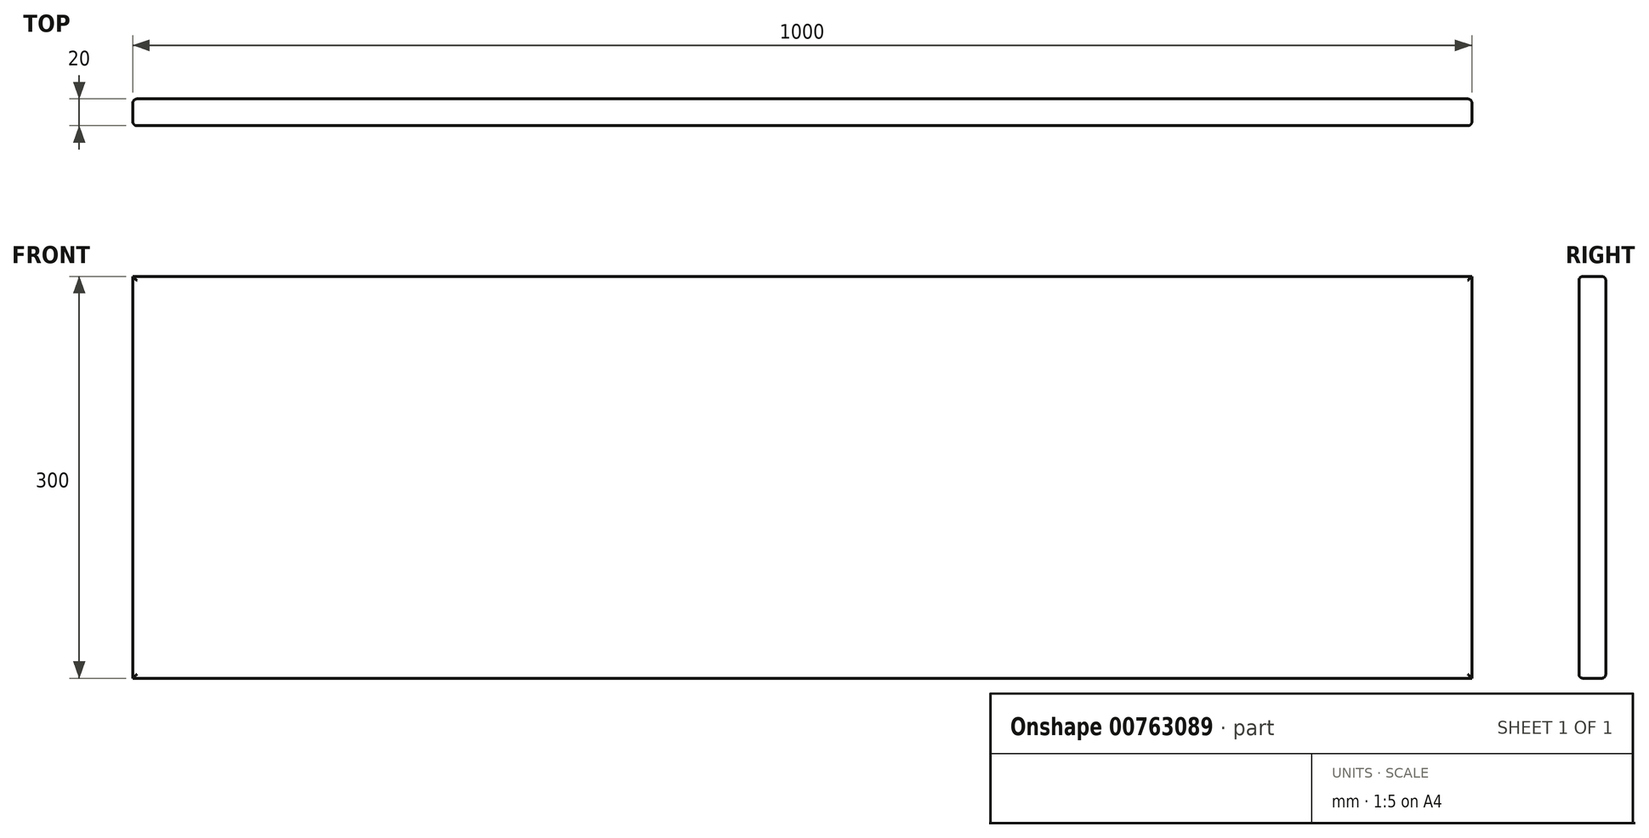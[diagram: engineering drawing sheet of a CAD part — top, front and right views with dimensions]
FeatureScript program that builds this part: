
annotation { "Feature Type Name" : "Feature", "Feature Type Description" : "" }
export const myFeature = defineFeature(function(context is Context, id is Id, definition is map)
    precondition{}
    {
        {
            var Q0;
            Q0=qCreatedBy(makeId("Front.planeOp"),FACE);
            var sketch = newSketch(context, id + "F0", { "sketchPlane" : qUnion([Q0])});
            skLineSegment(sketch, "E0.bottom", {"start": v(0, 0) * mm, "end": v(1000, 0) * mm});
            skLineSegment(sketch, "E0.top", {"start": v(0, 300) * mm, "end": v(1000, 300) * mm});
            skLineSegment(sketch, "E0.left", {"start": v(0, 0) * mm, "end": v(0, 300) * mm});
            skLineSegment(sketch, "E0.right", {"start": v(1000, 0) * mm, "end": v(1000, 300) * mm});
            skSolve(sketch);
        }
        {
            var Q0;
            Q0=makeQuery(id+"F0.imprint","IMPRINT",FACE,{"disambiguationData":[TD([[makeQuery(id+"F0.imprint","IMPRINT",EDGE,{"derivedFrom":sQuery(id+"F0.wireOp",EDGE,"E0.bottom")}),1.0]])]});
            extrude(context, id + "F1", {"entities" : qUnion([Q0]), "depth" : 20 * mm, "offsetDistance" : 25 * mm});
        }
        {
            var Q0;
            Q0=makeQuery(id+"F1.opExtrude","CAP_FACE",FACE,{"disambiguationData":[OSD([sQuery(id+"F0.wireOp",EDGE,"E0.bottom"),sQuery(id+"F0.wireOp",EDGE,"E0.top"),sQuery(id+"F0.wireOp",EDGE,"E0.left"),sQuery(id+"F0.wireOp",EDGE,"E0.right")])],"isStart":false});
            var Q1;
            Q1=makeQuery(id+"F1.opExtrude","CAP_FACE",FACE,{"disambiguationData":[OSD([sQuery(id+"F0.wireOp",EDGE,"E0.bottom"),sQuery(id+"F0.wireOp",EDGE,"E0.top"),sQuery(id+"F0.wireOp",EDGE,"E0.left"),sQuery(id+"F0.wireOp",EDGE,"E0.right")])],"isStart":true});
            fillet(context, id + "F2", {"entities" : qUnion([Q0, Q1]), "radius" : 3 * mm, "tangentPropagation" : true, "allowEdgeOverflow" : false});
        }
        {
            var Q0;
            Q0=makeQuery(id+"F1.opExtrude","CAP_FACE",FACE,{"disambiguationData":[OSD([sQuery(id+"F0.wireOp",EDGE,"E0.bottom"),sQuery(id+"F0.wireOp",EDGE,"E0.top"),sQuery(id+"F0.wireOp",EDGE,"E0.left"),sQuery(id+"F0.wireOp",EDGE,"E0.right")])],"isStart":false});
            var sketch = newSketch(context, id + "F3", { "sketchPlane" : qUnion([Q0])});
            skLineSegment(sketch, "E1", {"start": v(3, 297) * mm, "end": v(10.5, 297) * mm});
            skLineSegment(sketch, "E2", {"start": v(10.5, 297) * mm, "end": v(10.5, 215) * mm});
            skLineSegment(sketch, "E3", {"start": v(997, 297) * mm, "end": v(989.5, 297) * mm});
            skLineSegment(sketch, "E4", {"start": v(989.5, 297) * mm, "end": v(989.5, 215) * mm});
            skSolve(sketch);
        }
    });
